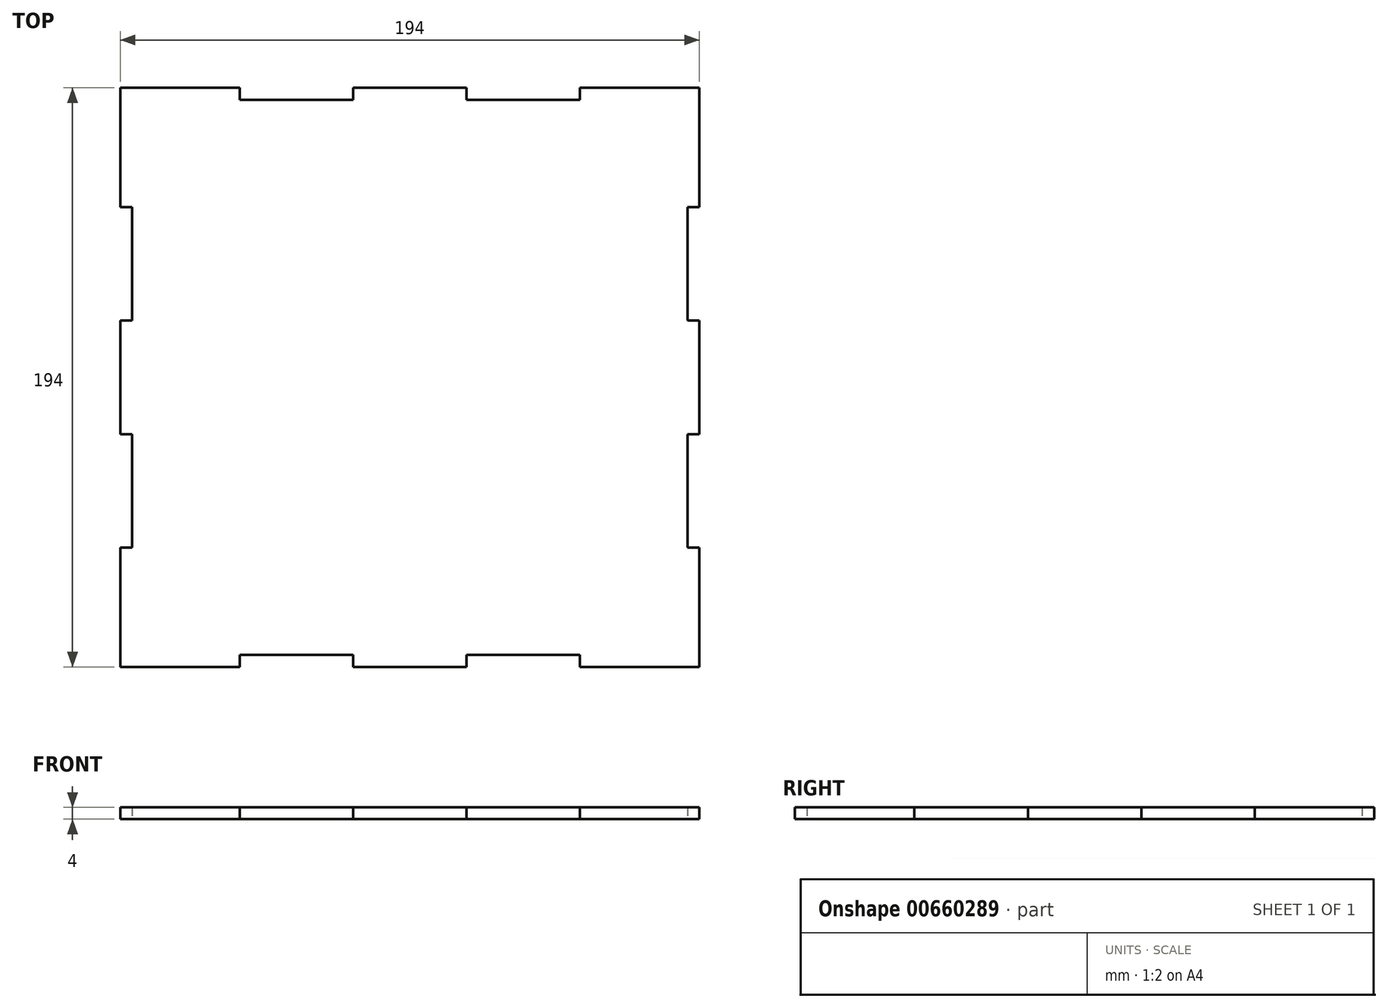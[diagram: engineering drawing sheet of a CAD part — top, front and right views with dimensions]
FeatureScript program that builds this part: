
annotation { "Feature Type Name" : "Feature", "Feature Type Description" : "" }
export const myFeature = defineFeature(function(context is Context, id is Id, definition is map)
    precondition{}
    {
        {
            var Q0;
            Q0=qCreatedBy(makeId("Top.planeOp"),FACE);
            var sketch = newSketch(context, id + "F0", { "sketchPlane" : qUnion([Q0])});
            skLineSegment(sketch, "E0.bottom", {"start": v(0, 0) * mm, "end": v(194, 0) * mm});
            skLineSegment(sketch, "E0.top", {"start": v(0, 194) * mm, "end": v(194, 194) * mm});
            skLineSegment(sketch, "E0.left", {"start": v(0, 0) * mm, "end": v(0, 194) * mm});
            skLineSegment(sketch, "E0.right", {"start": v(194, 0) * mm, "end": v(194, 194) * mm});
            skLineSegment(sketch, "E1.bottom", {"start": v(0, 154) * mm, "end": v(4, 154) * mm});
            skLineSegment(sketch, "E1.top", {"start": v(0, 116) * mm, "end": v(4, 116) * mm});
            skLineSegment(sketch, "E1.left", {"start": v(0, 154) * mm, "end": v(0, 116) * mm});
            skLineSegment(sketch, "E1.right", {"start": v(4, 154) * mm, "end": v(4, 116) * mm});
            skPoint(sketch, "E2.oppositeSnap0", {"position": v(4, 135) * mm});
            skLineSegment(sketch, "E2.bottom", {"start": v(0, 78) * mm, "end": v(4, 78) * mm});
            skLineSegment(sketch, "E2.top", {"start": v(0, 40) * mm, "end": v(4, 40) * mm});
            skLineSegment(sketch, "E2.left", {"start": v(0, 78) * mm, "end": v(0, 40) * mm});
            skLineSegment(sketch, "E2.right", {"start": v(4, 78) * mm, "end": v(4, 40) * mm});
            skLineSegment(sketch, "E3.bottom", {"start": v(40, 0) * mm, "end": v(78, 0) * mm});
            skLineSegment(sketch, "E3.top", {"start": v(40, 4) * mm, "end": v(78, 4) * mm});
            skLineSegment(sketch, "E3.left", {"start": v(40, 0) * mm, "end": v(40, 4) * mm});
            skLineSegment(sketch, "E3.right", {"start": v(78, 0) * mm, "end": v(78, 4) * mm});
            skLineSegment(sketch, "E4.bottom", {"start": v(116, 0) * mm, "end": v(154, 0) * mm});
            skLineSegment(sketch, "E4.top", {"start": v(116, 4) * mm, "end": v(154, 4) * mm});
            skLineSegment(sketch, "E4.left", {"start": v(116, 0) * mm, "end": v(116, 4) * mm});
            skLineSegment(sketch, "E4.right", {"start": v(154, 0) * mm, "end": v(154, 4) * mm});
            skLineSegment(sketch, "E5.bottom", {"start": v(194, 40) * mm, "end": v(190, 40) * mm});
            skLineSegment(sketch, "E5.top", {"start": v(194, 78) * mm, "end": v(190, 78) * mm});
            skLineSegment(sketch, "E5.left", {"start": v(194, 40) * mm, "end": v(194, 78) * mm});
            skLineSegment(sketch, "E5.right", {"start": v(190, 40) * mm, "end": v(190, 78) * mm});
            skLineSegment(sketch, "E6.bottom", {"start": v(194, 116) * mm, "end": v(190, 116) * mm});
            skLineSegment(sketch, "E6.top", {"start": v(194, 154) * mm, "end": v(190, 154) * mm});
            skLineSegment(sketch, "E6.left", {"start": v(194, 116) * mm, "end": v(194, 154) * mm});
            skLineSegment(sketch, "E6.right", {"start": v(190, 116) * mm, "end": v(190, 154) * mm});
            skLineSegment(sketch, "E7.bottom", {"start": v(154, 194) * mm, "end": v(116, 194) * mm});
            skLineSegment(sketch, "E7.top", {"start": v(154, 190) * mm, "end": v(116, 190) * mm});
            skLineSegment(sketch, "E7.left", {"start": v(154, 194) * mm, "end": v(154, 190) * mm});
            skLineSegment(sketch, "E7.right", {"start": v(116, 194) * mm, "end": v(116, 190) * mm});
            skLineSegment(sketch, "E8.bottom", {"start": v(78, 194) * mm, "end": v(40, 194) * mm});
            skLineSegment(sketch, "E8.top", {"start": v(78, 190) * mm, "end": v(40, 190) * mm});
            skLineSegment(sketch, "E8.left", {"start": v(78, 194) * mm, "end": v(78, 190) * mm});
            skLineSegment(sketch, "E8.right", {"start": v(40, 194) * mm, "end": v(40, 190) * mm});
            skSolve(sketch);
        }
        {
            var Q0;
            {var subQ2=sQuery(id+"F0.wireOp",EDGE,"E1.bottom");Q0=makeQuery(id+"F0.imprint","IMPRINT",FACE,{"disambiguationData":[TD([[makeQuery(id+"F0.imprint","IMPRINT",EDGE,{"derivedFrom":subQ2}),1.0]])]});}
            extrude(context, id + "F1", {"entities" : qUnion([Q0]), "depth" : 4 * mm, "offsetDistance" : 25 * mm});
        }
    });
